# Revit family: Faucet_Touchless-Lavatory-KOHLER-Accliv-K-30276X.rfa_
name_source: partatom
category: Plumbing Fixtures
units: mm (PartAtom-declared; Revit-internal decimal feet)

## family parameters
Cut with Voids When Loaded = No
Host = Face
OmniClass Number = 23.31.11.00
OmniClass Title = Faucets
Part Type = Normal
Room Calculation Point = No
Round Connector Dimension = Use Diameter
Shared = No

## types (3) — shared parameters
ADA Compliant = No
Apparent Load = 0 VA
Assembly Code = D2010
CW Connection = Yes
Cold Water Inlet = Cold Water Inlet
Date Modified = 06/06/2023
Default Elevation = 36"
Drain Included = No
Electrical Connector = Yes
Electrical Note = One Dedicated Circuit Required
Finish = Kohler-Metal-CP-Polished_Chrome
HW Connection = No
Height = 4 11/16"
Hot Water Inlet = Hot Water Inlet
Length = 4"
Manufacturer = Kohler Co.
Master Format 2014 = 22 41 39
Master Format 2014 Name = Residential Faucets, Supplies, and Trim
Material = Premium Metal Construction
Pressure = 0.00 psi
Product Name = Accliv
Spout Reach = 4"
URL = https://www.kohler.co.th
Vent Connection = No
Voltage = 220 V
Waste Connection = No
Waste Water Outlet = Waste Water Outlet
WaterSense Certified = No
Width = 1 15/16"

## per-type parameters (varying)
| type | Description | Flow Rate | Model | Type |
| 0.5 GPM, CP-Polished Chrome | Sensor Faucet Cold 0.5GPM No Drain | 1 GPM | K-30276X-CP | 1 |
| 0.35 GPM, CP-Polished Chrome | Sensor Faucet Cold 0.35GPM No Drain | 0 GPM | K-30276X-S3-CP | 2 |
| 0.26 GPM, CP-Polished Chrome | Sensor Faucet Cold 0.26GPM No Drain | 0 GPM | K-30276X-S5-CP | 3 |

## geometry (parser evidence)
native form markers: Sweep x5
no freeform markers — native parametric forms only
